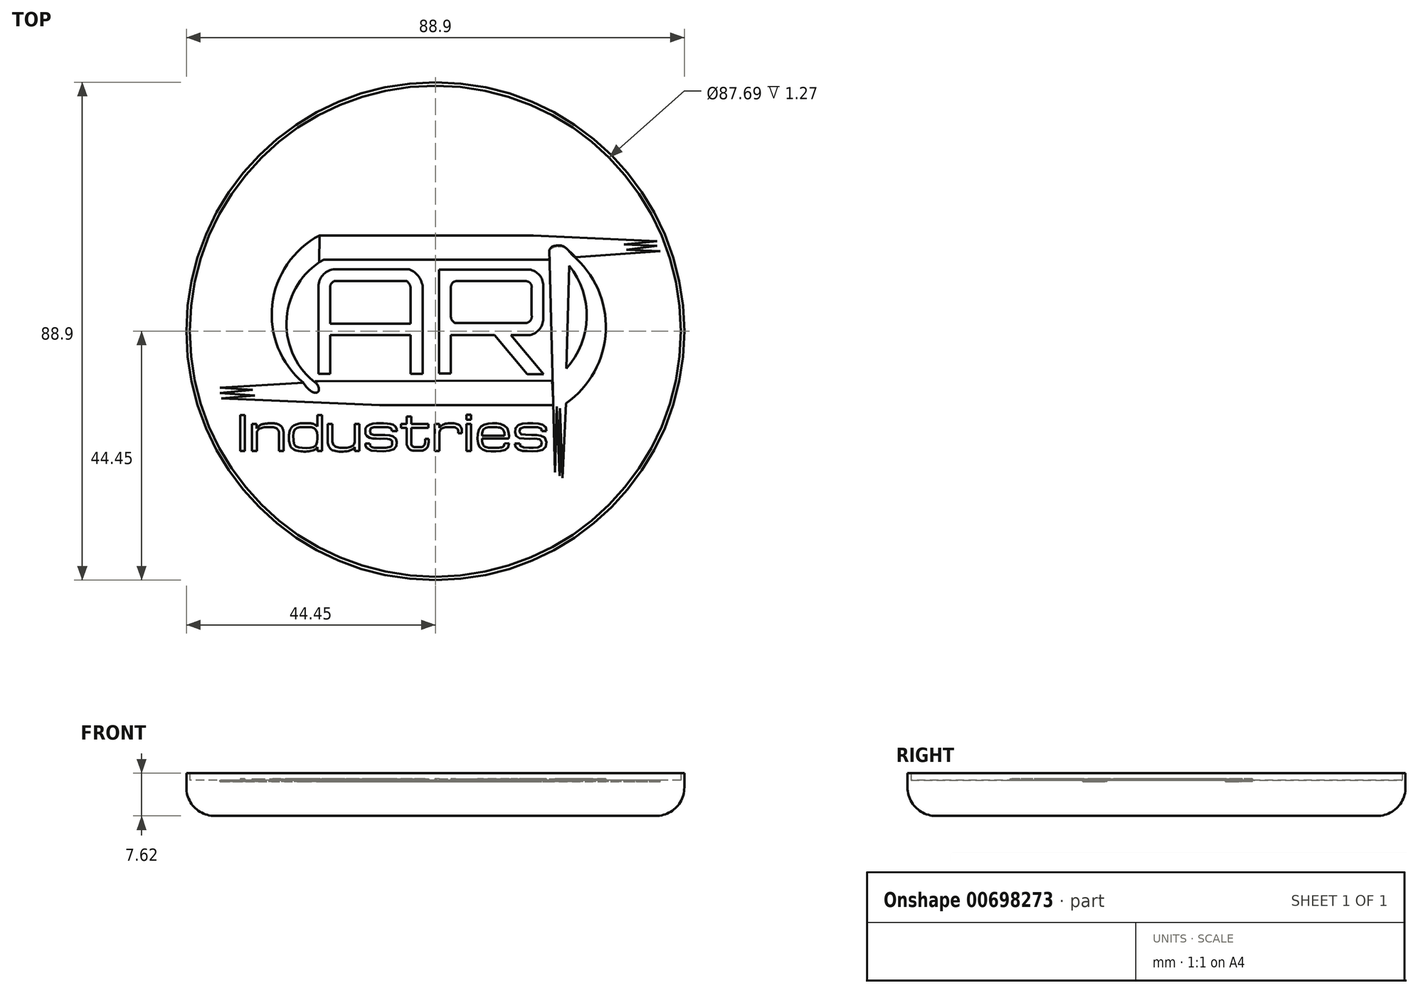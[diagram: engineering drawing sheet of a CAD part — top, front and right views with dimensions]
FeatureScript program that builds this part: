
annotation { "Feature Type Name" : "Feature", "Feature Type Description" : "" }
export const myFeature = defineFeature(function(context is Context, id is Id, definition is map)
    precondition{}
    {
        {
            var Q0;
            Q0=qCreatedBy(makeId("Top.planeOp"),FACE);
            var sketch = newSketch(context, id + "F0", { "sketchPlane" : qUnion([Q0])});
            skCircle(sketch, "E0", {"center": v(0, 0) * mm, "radius": 44.45 * mm});
            skSolve(sketch);
        }
        {
            var Q0;
            Q0=makeQuery(id+"F0.imprint","IMPRINT",FACE,{"disambiguationData":[TD([[makeQuery(id+"F0.imprint","IMPRINT",EDGE,{"derivedFrom":sQuery(id+"F0.wireOp",EDGE,"E0")}),1.0]])]});
            var Q1;
            Q1 = qSketchRegion(id + "FZvUu5gdxCIZSAn_1", true);
            extrude(context, id + "F1", {"entities" : qUnion([Q0, Q1]), "depth" : 6.35 * mm, "offsetDistance" : 25.4 * mm});
        }
        {
            var Q0;
            Q0=makeQuery(id+"F1.opExtrude","CAP_FACE",FACE,{"disambiguationData":[OSD([sQuery(id+"F0.wireOp",EDGE,"E0")])],"isStart":false});
            var sketch = newSketch(context, id + "F2", { "sketchPlane" : qUnion([Q0])});
            skLineSegment(sketch, "E1", {"start": v(-20.68, 17.1) * mm, "end": v(3.27, 17.1) * mm});
            skLineSegment(sketch, "E2", {"start": v(3.27, 17.1) * mm, "end": v(17.5, 17.1) * mm});
            skLineSegment(sketch, "E3", {"start": v(17.5, 17.1) * mm, "end": v(39.6, 16.1) * mm});
            skLineSegment(sketch, "E4", {"start": v(39.6, 16.1) * mm, "end": v(33.68, 15.49) * mm});
            skLineSegment(sketch, "E5", {"start": v(33.68, 15.49) * mm, "end": v(39.6, 15.22) * mm});
            skLineSegment(sketch, "E6", {"start": v(39.6, 15.22) * mm, "end": v(34.13, 14.55) * mm});
            skLineSegment(sketch, "E7", {"start": v(34.13, 14.55) * mm, "end": v(40.17, 14.28) * mm});
            skLineSegment(sketch, "E8", {"start": v(40.17, 14.28) * mm, "end": v(25.05, 13.22) * mm});
            skLineSegment(sketch, "E9", {"start": v(21.09, -13.18) * mm, "end": v(-9.93, -13.18) * mm});
            skLineSegment(sketch, "E10", {"start": v(-9.93, -13.18) * mm, "end": v(-38.2, -12.01) * mm});
            skLineSegment(sketch, "E11", {"start": v(-38.2, -12.01) * mm, "end": v(-32.22, -11.47) * mm});
            skLineSegment(sketch, "E12", {"start": v(-32.22, -11.47) * mm, "end": v(-38.47, -11.07) * mm});
            skLineSegment(sketch, "E13", {"start": v(-38.47, -11.07) * mm, "end": v(-32.61, -10.5) * mm});
            skLineSegment(sketch, "E14", {"start": v(-32.61, -10.5) * mm, "end": v(-38.47, -10.12) * mm});
            skLineSegment(sketch, "E15", {"start": v(-38.47, -10.12) * mm, "end": v(-23.55, -9.23) * mm});
            skLineSegment(sketch, "E16", {"start": v(-19.94, 12.8) * mm, "end": v(20.37, 12.8) * mm});
            skLineSegment(sketch, "E17", {"start": v(20.88, -8.84) * mm, "end": v(-20.9, -8.96) * mm});
            skLineSegment(sketch, "E18", {"start": v(-20.9, -8.96) * mm, "end": v(-21.48, -8.96) * mm});
            skFitSpline(sketch, "E19", {"points": [v(-23.55, -9.23) * mm, v(-23.04, -9.94) * mm, v(-22.45, -10.52) * mm, v(-21.73, -10.94) * mm, v(-21.12, -10.94) * mm, v(-20.8, -10.55) * mm, v(-20.83, -10.06) * mm, v(-21.15, -9.42) * mm, v(-21.48, -8.96) * mm], "startDerivative": vector(3.5, -5.09) * mm, "endDerivative": vector(-0.03, 4.48) * mm});
            skFitSpline(sketch, "E20", {"points": [v(-20.71, 12.3) * mm, v(-19.94, 12.8) * mm], "startDerivative": vector(0.78, 0.5) * mm, "endDerivative": vector(0.78, 0.5) * mm});
            skLineSegment(sketch, "E21", {"start": v(-20.68, 17.1) * mm, "end": v(-20.71, 12.3) * mm});
            skLineSegment(sketch, "E22", {"start": v(20.88, -8.84) * mm, "end": v(21.09, -13.18) * mm});
            skLineSegment(sketch, "E23", {"start": v(20.37, 12.8) * mm, "end": v(20.37, 14.57) * mm});
            skFitSpline(sketch, "E24", {"points": [v(25.05, 13.22) * mm, v(23.55, 14.57) * mm, v(22.5, 15.06) * mm, v(21.77, 15.06) * mm, v(21.45, 15.06) * mm, v(20.37, 14.57) * mm], "startDerivative": vector(-5.42, 5.3) * mm, "endDerivative": vector(-5.79, -3.03) * mm});
            skSolve(sketch);
        }
        {
            var Q0;
            Q0 = qSketchRegion(id + "F2", true);
            extrude(context, id + "F3", {"entities" : qUnion([Q0]), "operationType" : NewBodyOperationType.REMOVE, "oppositeDirection" : true, "depth" : 0.25 * mm, "offsetDistance" : 25.4 * mm});
        }
        {
            var Q0;
            Q0=makeQuery(id+"F1.opExtrude","CAP_FACE",FACE,{"disambiguationData":[OSD([sQuery(id+"F0.wireOp",EDGE,"E0")])],"isStart":false});
            var sketch = newSketch(context, id + "F4", { "sketchPlane" : qUnion([Q0])});
            skLineSegment(sketch, "E25", {"start": v(-18.77, 1.36) * mm, "end": v(-4.4, 1.36) * mm});
            skLineSegment(sketch, "E26", {"start": v(-4.4, 1.36) * mm, "end": v(-4.4, 7.49) * mm});
            skLineSegment(sketch, "E27", {"start": v(-18.77, 1.36) * mm, "end": v(-18.77, 7.88) * mm});
            skLineSegment(sketch, "E28", {"start": v(-18.77, -0.72) * mm, "end": v(-4.4, -0.72) * mm});
            skLineSegment(sketch, "E29", {"start": v(-4.4, -0.72) * mm, "end": v(-4.4, -7.63) * mm});
            skLineSegment(sketch, "E30", {"start": v(-18.77, -0.72) * mm, "end": v(-18.77, -7.63) * mm});
            skLineSegment(sketch, "E31", {"start": v(-18.77, -7.63) * mm, "end": v(-20.85, -7.63) * mm});
            skLineSegment(sketch, "E32", {"start": v(-20.85, -7.63) * mm, "end": v(-20.85, 7.97) * mm});
            skLineSegment(sketch, "E33", {"start": v(-4.4, -7.63) * mm, "end": v(-2.24, -7.63) * mm});
            skLineSegment(sketch, "E34", {"start": v(-2.24, -7.63) * mm, "end": v(-2.24, 7.54) * mm});
            skLineSegment(sketch, "E35", {"start": v(-18.02, 8.94) * mm, "end": v(-5.08, 8.94) * mm});
            skLineSegment(sketch, "E36", {"start": v(-4.67, 11.06) * mm, "end": v(-18.22, 11.06) * mm});
            skArc(sketch, "E37", {"start": v(-18.22, 11.06) * mm, "mid": v(-20.1, 10) * mm, "end": v(-20.85, 7.97) * mm});
            skArc(sketch, "E38", {"start": v(-2.24, 7.54) * mm, "mid": v(-2.9, 9.68) * mm, "end": v(-4.67, 11.06) * mm});
            skArc(sketch, "E39", {"start": v(-18.02, 8.94) * mm, "mid": v(-18.56, 8.53) * mm, "end": v(-18.77, 7.88) * mm});
            skArc(sketch, "E40", {"start": v(-4.4, 7.49) * mm, "mid": v(-4.57, 8.3) * mm, "end": v(-5.08, 8.94) * mm});
            skLineSegment(sketch, "E41", {"start": v(0.66, -7.53) * mm, "end": v(0.66, 11.02) * mm});
            skLineSegment(sketch, "E42", {"start": v(0.66, 11.02) * mm, "end": v(16.82, 11.02) * mm});
            skLineSegment(sketch, "E43", {"start": v(0.66, -7.53) * mm, "end": v(2.78, -7.53) * mm});
            skLineSegment(sketch, "E44", {"start": v(2.78, -7.53) * mm, "end": v(2.78, -0.67) * mm});
            skLineSegment(sketch, "E45", {"start": v(2.78, -0.67) * mm, "end": v(10.6, -0.67) * mm});
            skLineSegment(sketch, "E46", {"start": v(10.6, -0.67) * mm, "end": v(16.44, -7.68) * mm});
            skLineSegment(sketch, "E47", {"start": v(16.44, -7.68) * mm, "end": v(19.3, -7.68) * mm});
            skLineSegment(sketch, "E48", {"start": v(19.3, -7.68) * mm, "end": v(13.47, -0.67) * mm});
            skLineSegment(sketch, "E49", {"start": v(13.47, -0.67) * mm, "end": v(16.92, -0.67) * mm});
            skLineSegment(sketch, "E50", {"start": v(19.27, 8.12) * mm, "end": v(19.27, 2.23) * mm});
            skLineSegment(sketch, "E51", {"start": v(3.6, 1.45) * mm, "end": v(16.07, 1.45) * mm});
            skLineSegment(sketch, "E52", {"start": v(3.67, 8.94) * mm, "end": v(16.17, 8.94) * mm});
            skLineSegment(sketch, "E53", {"start": v(2.78, 7.88) * mm, "end": v(2.78, 2.61) * mm});
            skLineSegment(sketch, "E54", {"start": v(17.2, 7.68) * mm, "end": v(17.2, 2.85) * mm});
            skArc(sketch, "E55", {"start": v(3.67, 8.94) * mm, "mid": v(3.03, 8.57) * mm, "end": v(2.78, 7.88) * mm});
            skArc(sketch, "E56", {"start": v(2.78, 2.61) * mm, "mid": v(3, 1.9) * mm, "end": v(3.6, 1.45) * mm});
            skArc(sketch, "E57", {"start": v(16.07, 1.45) * mm, "mid": v(16.97, 1.88) * mm, "end": v(17.2, 2.85) * mm});
            skArc(sketch, "E58", {"start": v(17.2, 7.68) * mm, "mid": v(16.98, 8.55) * mm, "end": v(16.17, 8.94) * mm});
            skArc(sketch, "E59", {"start": v(16.92, -0.67) * mm, "mid": v(18.61, 0.36) * mm, "end": v(19.27, 2.23) * mm});
            skArc(sketch, "E60", {"start": v(19.27, 8.12) * mm, "mid": v(18.58, 10.02) * mm, "end": v(16.82, 11.02) * mm});
            skLineSegment(sketch, "E61", {"start": v(20.33, 14.53) * mm, "end": v(21.4, -25.19) * mm});
            skFitSpline(sketch, "E62", {"points": [v(20.33, 14.53) * mm, v(20.8, 15.06) * mm, v(21.4, 15.26) * mm, v(22.3, 15.32) * mm, v(23.05, 15.06) * mm, v(23.66, 14.53) * mm, v(24.46, 13.6) * mm], "startDerivative": vector(2.83, 4) * mm, "endDerivative": vector(4.08, -4.92) * mm});
            skArc(sketch, "E63", {"start": v(23.33, -12.88) * mm, "mid": v(30.43, 0.08) * mm, "end": v(24.46, 13.6) * mm});
            skLineSegment(sketch, "E64", {"start": v(23.33, -12.88) * mm, "end": v(22.72, -26.2) * mm});
            skLineSegment(sketch, "E65", {"start": v(22.72, -26.2) * mm, "end": v(22.27, -13.79) * mm});
            skLineSegment(sketch, "E66", {"start": v(22.16, -25.83) * mm, "end": v(22.27, -13.79) * mm});
            skLineSegment(sketch, "E67", {"start": v(22.16, -25.83) * mm, "end": v(21.71, -13.48) * mm});
            skLineSegment(sketch, "E68", {"start": v(21.71, -13.48) * mm, "end": v(21.4, -25.19) * mm});
            skArc(sketch, "E69", {"start": v(-20.71, 12.3) * mm, "mid": v(-26.58, 1.62) * mm, "end": v(-21.23, -9.33) * mm});
            skArc(sketch, "E70", {"start": v(-20.68, 17.1) * mm, "mid": v(-29.12, 4.7) * mm, "end": v(-23.55, -9.23) * mm});
            skLineSegment(sketch, "E71", {"start": v(23.88, 11.71) * mm, "end": v(23.42, -6.67) * mm});
            skArc(sketch, "E72", {"start": v(23.42, -6.67) * mm, "mid": v(27.02, 2.44) * mm, "end": v(23.88, 11.71) * mm});
            skFitSpline(sketch, "E73", {"points": [v(-23.55, -9.23) * mm, v(-23.5, -9.32) * mm, v(-23.36, -9.5) * mm, v(-23.2, -9.72) * mm, v(-22.93, -10.06) * mm, v(-22.67, -10.33) * mm, v(-22.48, -10.5) * mm, v(-22.2, -10.71) * mm, v(-22.09, -10.78) * mm, v(-21.93, -10.87) * mm, v(-21.68, -10.96) * mm, v(-21.44, -11) * mm, v(-21.24, -10.98) * mm], "startDerivative": vector(1, -1.41) * mm, "endDerivative": vector(4.4, 0.6) * mm});
            skFitSpline(sketch, "E74", {"points": [v(-21.24, -10.98) * mm, v(-21.2, -10.97) * mm, v(-21.14, -10.95) * mm, v(-21.08, -10.92) * mm, v(-21.03, -10.9) * mm, v(-21, -10.86) * mm, v(-20.94, -10.8) * mm, v(-20.9, -10.76) * mm, v(-20.88, -10.73) * mm, v(-20.86, -10.7) * mm, v(-20.84, -10.66) * mm, v(-20.82, -10.61) * mm, v(-20.8, -10.56) * mm, v(-20.79, -10.5) * mm, v(-20.78, -10.46) * mm, v(-20.78, -10.42) * mm, v(-20.78, -10.37) * mm, v(-20.78, -10.33) * mm], "startDerivative": vector(0.82, 0.2) * mm, "endDerivative": vector(-0.02, 0.76) * mm});
            skFitSpline(sketch, "E75", {"points": [v(-20.78, -10.33) * mm, v(-20.78, -10.28) * mm, v(-20.8, -10.23) * mm, v(-20.8, -10.2) * mm, v(-20.8, -10.15) * mm, v(-20.82, -10.12) * mm, v(-20.83, -10.07) * mm, v(-20.84, -10.02) * mm, v(-20.86, -9.98) * mm, v(-20.88, -9.91) * mm, v(-20.9, -9.86) * mm, v(-20.92, -9.81) * mm, v(-20.92, -9.8) * mm, v(-20.94, -9.77) * mm, v(-20.96, -9.73) * mm, v(-20.98, -9.67) * mm, v(-21.01, -9.62) * mm, v(-21.04, -9.56) * mm, v(-21.07, -9.53) * mm, v(-21.1, -9.48) * mm, v(-21.14, -9.43) * mm, v(-21.17, -9.4) * mm, v(-21.2, -9.36) * mm, v(-21.23, -9.33) * mm], "startDerivative": vector(-0.1, 0.98) * mm, "endDerivative": vector(-0.64, 0.65) * mm});
            skFitSpline(sketch, "E76", {"points": [v(-20.68, 17.1) * mm, v(-20.68, 16.62) * mm, v(-20.69, 16) * mm, v(-20.7, 15.36) * mm, v(-20.7, 14.4) * mm, v(-20.7, 12.75) * mm, v(-20.71, 12.48) * mm, v(-20.71, 12.3) * mm], "startDerivative": vector(-0.03, -3.67) * mm, "endDerivative": vector(-0.02, -2.42) * mm});
            skSolve(sketch);
        }
        {
            var Q0;
            Q0 = qSketchRegion(id + "F4", true);
            extrude(context, id + "F5", {"entities" : qUnion([Q0]), "operationType" : NewBodyOperationType.ADD, "depth" : 0.25 * mm, "offsetDistance" : 25.4 * mm});
        }
        {
            var Q0;
            Q0=makeQuery(id+"F1.opExtrude","CAP_FACE",FACE,{"disambiguationData":[OSD([sQuery(id+"F0.wireOp",EDGE,"E0")])],"isStart":false});
            var sketch = newSketch(context, id + "F6", { "sketchPlane" : qUnion([Q0])});
            skLineSegment(sketch, "E77", {"start": v(-34.85, -21.38) * mm, "end": v(-34.85, -14.96) * mm});
            skLineSegment(sketch, "E78", {"start": v(-34.85, -14.96) * mm, "end": v(-33.98, -14.96) * mm});
            skLineSegment(sketch, "E79", {"start": v(-33.98, -14.96) * mm, "end": v(-33.98, -21.38) * mm});
            skLineSegment(sketch, "E80", {"start": v(-33.98, -21.38) * mm, "end": v(-34.85, -21.38) * mm});
            skLineSegment(sketch, "E81", {"start": v(-32.7, -16.6) * mm, "end": v(-31.9, -16.6) * mm});
            skLineSegment(sketch, "E82", {"start": v(-31.9, -16.6) * mm, "end": v(-31.9, -17.36) * mm});
            skLineSegment(sketch, "E83", {"start": v(-32.7, -16.6) * mm, "end": v(-32.7, -21.38) * mm});
            skLineSegment(sketch, "E84", {"start": v(-32.7, -21.38) * mm, "end": v(-31.87, -21.38) * mm});
            skLineSegment(sketch, "E85", {"start": v(-31.87, -21.38) * mm, "end": v(-31.87, -18.15) * mm});
            skPoint(sketch, "E86.2.internal.snap0", {"position": v(-31.9, -16.98) * mm});
            skFitSpline(sketch, "E86", {"points": [v(-31.9, -17.36) * mm, v(-31.73, -17.14) * mm, v(-31.54, -16.98) * mm, v(-31.28, -16.77) * mm, v(-30.94, -16.63) * mm, v(-30.5, -16.54) * mm, v(-29.97, -16.47) * mm, v(-29.48, -16.45) * mm], "startDerivative": vector(1.34, 1.97) * mm, "endDerivative": vector(3.55, -0.7) * mm});
            skFitSpline(sketch, "E87", {"points": [v(-29.48, -16.45) * mm, v(-29.19, -16.45) * mm, v(-28.9, -16.45) * mm, v(-28.61, -16.48) * mm, v(-28.28, -16.55) * mm, v(-27.85, -16.73) * mm, v(-27.49, -17) * mm, v(-27.25, -17.4) * mm, v(-27.12, -17.9) * mm, v(-27.1, -18.05) * mm], "startDerivative": vector(2.88, -0.02) * mm, "endDerivative": vector(0.29, -1.67) * mm});
            skFitSpline(sketch, "E88", {"points": [v(-31.87, -18.15) * mm, v(-31.83, -17.95) * mm, v(-31.72, -17.74) * mm, v(-31.59, -17.57) * mm, v(-31.28, -17.35) * mm, v(-30.93, -17.23) * mm, v(-30.62, -17.16) * mm, v(-30.06, -17.14) * mm, v(-29.44, -17.14) * mm, v(-29.03, -17.15) * mm, v(-28.76, -17.19) * mm, v(-28.4, -17.33) * mm, v(-28.16, -17.52) * mm, v(-28.03, -17.7) * mm, v(-27.92, -18.04) * mm, v(-27.9, -18.15) * mm], "startDerivative": vector(0.57, 3.72) * mm, "endDerivative": vector(0.27, -2.24) * mm});
            skLineSegment(sketch, "E89", {"start": v(-27.9, -18.15) * mm, "end": v(-27.9, -21.38) * mm});
            skLineSegment(sketch, "E90", {"start": v(-27.9, -21.38) * mm, "end": v(-27.1, -21.38) * mm});
            skLineSegment(sketch, "E91", {"start": v(-27.1, -21.38) * mm, "end": v(-27.1, -18.05) * mm});
            skLineSegment(sketch, "E92", {"start": v(-21.05, -20.7) * mm, "end": v(-21.05, -21.38) * mm});
            skLineSegment(sketch, "E93", {"start": v(-21.05, -21.38) * mm, "end": v(-20.24, -21.38) * mm});
            skLineSegment(sketch, "E94", {"start": v(-20.24, -21.38) * mm, "end": v(-20.24, -14.99) * mm});
            skLineSegment(sketch, "E95", {"start": v(-20.24, -14.99) * mm, "end": v(-21.05, -14.99) * mm});
            skLineSegment(sketch, "E96", {"start": v(-21.05, -14.99) * mm, "end": v(-21.05, -17.01) * mm});
            skArc(sketch, "E97", {"start": v(-21.05, -17.01) * mm, "mid": v(-21.78, -16.57) * mm, "end": v(-22.62, -16.46) * mm});
            skLineSegment(sketch, "E98", {"start": v(-22.62, -16.46) * mm, "end": v(-23.76, -16.46) * mm});
            skFitSpline(sketch, "E99", {"points": [v(-23.76, -16.46) * mm, v(-24.06, -16.46) * mm, v(-24.51, -16.53) * mm, v(-24.87, -16.65) * mm, v(-25.16, -16.77) * mm, v(-25.47, -16.97) * mm, v(-25.7, -17.21) * mm, v(-25.84, -17.48) * mm, v(-25.97, -17.78) * mm, v(-26.08, -18.23) * mm, v(-26.12, -18.65) * mm, v(-26.12, -19.1) * mm, v(-26.11, -19.6) * mm], "startDerivative": vector(-3.77, 0.16) * mm, "endDerivative": vector(-0.26, -4.85) * mm});
            skFitSpline(sketch, "E100", {"points": [v(-26.11, -19.6) * mm, v(-26.05, -19.97) * mm, v(-25.93, -20.39) * mm, v(-25.66, -20.82) * mm, v(-25.17, -21.18) * mm, v(-24.56, -21.37) * mm, v(-23.77, -21.47) * mm, v(-23.19, -21.5) * mm, v(-22.56, -21.46) * mm, v(-22.02, -21.32) * mm, v(-21.5, -21.14) * mm, v(-21.19, -20.87) * mm, v(-21.05, -20.7) * mm], "startDerivative": vector(0.84, -5.24) * mm, "endDerivative": vector(2.18, 3.02) * mm});
            skFitSpline(sketch, "E101", {"points": [v(-24.16, -17.16) * mm, v(-23.2, -17.14) * mm, v(-22.46, -17.12) * mm, v(-22, -17.17) * mm, v(-21.62, -17.33) * mm, v(-21.36, -17.57) * mm, v(-21.19, -17.9) * mm, v(-21.1, -18.35) * mm, v(-21.05, -18.85) * mm, v(-21.05, -19.34) * mm, v(-21.14, -19.96) * mm, v(-21.39, -20.43) * mm, v(-21.75, -20.7) * mm, v(-22.38, -20.85) * mm, v(-23.12, -20.87) * mm, v(-24.08, -20.83) * mm, v(-24.5, -20.75) * mm, v(-25.01, -20.47) * mm, v(-25.27, -20.03) * mm, v(-25.34, -19.18) * mm, v(-25.34, -18.43) * mm, v(-25.27, -17.9) * mm, v(-25.01, -17.5) * mm, v(-24.64, -17.26) * mm, v(-24.16, -17.16) * mm]});
            skLineSegment(sketch, "E102", {"start": v(-12.5, -20.05) * mm, "end": v(-11.7, -20.05) * mm});
            skLineSegment(sketch, "E103", {"start": v(-7.71, -17.84) * mm, "end": v(-6.85, -17.84) * mm});
            skFitSpline(sketch, "E104", {"points": [v(-12.5, -20.05) * mm, v(-12.5, -20.22) * mm, v(-12.5, -20.41) * mm], "startDerivative": vector(0, -0.43) * mm, "endDerivative": vector(0, -0.53) * mm});
            skFitSpline(sketch, "E105", {"points": [v(-12.5, -20.41) * mm, v(-12.4, -20.6) * mm, v(-12.26, -20.84) * mm, v(-11.65, -21.23) * mm, v(-10.81, -21.4) * mm, v(-9.83, -21.44) * mm, v(-8.64, -21.4) * mm, v(-7.8, -21.26) * mm, v(-7.3, -21.02) * mm, v(-6.98, -20.61) * mm, v(-6.9, -20.04) * mm, v(-6.9, -19.72) * mm, v(-6.95, -19.39) * mm, v(-7.16, -19.05) * mm, v(-7.52, -18.78) * mm, v(-7.85, -18.65) * mm, v(-8.27, -18.58) * mm, v(-8.9, -18.56) * mm, v(-9.83, -18.54) * mm, v(-10.74, -18.52) * mm, v(-11.2, -18.48) * mm, v(-11.48, -18.4) * mm, v(-11.64, -18.23) * mm, v(-11.67, -17.94) * mm, v(-11.67, -17.65) * mm, v(-11.57, -17.42) * mm, v(-11.34, -17.26) * mm, v(-11.05, -17.17) * mm, v(-10.42, -17.14) * mm, v(-9.88, -17.13) * mm, v(-9.2, -17.14) * mm, v(-8.65, -17.15) * mm, v(-8.24, -17.2) * mm, v(-7.93, -17.31) * mm, v(-7.74, -17.54) * mm, v(-7.71, -17.84) * mm], "startDerivative": vector(5.04, -9.49) * mm, "endDerivative": vector(-0.58, -13.71) * mm});
            skFitSpline(sketch, "E106", {"points": [v(-6.85, -17.84) * mm, v(-6.85, -17.7) * mm, v(-6.9, -17.42) * mm, v(-7.03, -17.14) * mm, v(-7.33, -16.83) * mm, v(-7.6, -16.7) * mm, v(-8.08, -16.55) * mm, v(-8.51, -16.5) * mm, v(-8.96, -16.47) * mm, v(-9.72, -16.46) * mm, v(-10.27, -16.45) * mm, v(-10.7, -16.47) * mm, v(-11.32, -16.54) * mm, v(-11.77, -16.7) * mm, v(-12.1, -16.9) * mm, v(-12.36, -17.19) * mm, v(-12.5, -17.47) * mm, v(-12.5, -17.84) * mm, v(-12.5, -18.25) * mm, v(-12.42, -18.5) * mm, v(-12.2, -18.78) * mm, v(-11.81, -19.03) * mm, v(-11.27, -19.15) * mm, v(-10.79, -19.2) * mm, v(-10.16, -19.2) * mm, v(-9.5, -19.2) * mm, v(-8.83, -19.2) * mm, v(-8.45, -19.24) * mm, v(-8.25, -19.27) * mm, v(-7.93, -19.37) * mm, v(-7.79, -19.5) * mm], "startDerivative": vector(0.37, 6.56) * mm, "endDerivative": vector(3.58, -6.96) * mm});
            skFitSpline(sketch, "E107", {"points": [v(-7.79, -19.5) * mm, v(-7.74, -19.57) * mm, v(-7.7, -19.72) * mm, v(-7.7, -20) * mm, v(-7.7, -20.22) * mm, v(-7.79, -20.45) * mm, v(-7.97, -20.63) * mm, v(-8.39, -20.75) * mm, v(-8.96, -20.8) * mm, v(-9.6, -20.83) * mm, v(-10.24, -20.83) * mm, v(-10.7, -20.82) * mm, v(-11.16, -20.74) * mm, v(-11.44, -20.62) * mm, v(-11.62, -20.4) * mm, v(-11.66, -20.2) * mm, v(-11.7, -20.05) * mm], "startDerivative": vector(1.56, -1.96) * mm, "endDerivative": vector(-1.06, 3.3) * mm});
            skLineSegment(sketch, "E108", {"start": v(-4.27, -20.02) * mm, "end": v(-4.27, -17.25) * mm});
            skLineSegment(sketch, "E109", {"start": v(-4.27, -17.25) * mm, "end": v(-1.27, -17.25) * mm});
            skLineSegment(sketch, "E110", {"start": v(-1.27, -17.25) * mm, "end": v(-1.27, -16.57) * mm});
            skLineSegment(sketch, "E111", {"start": v(-1.27, -16.57) * mm, "end": v(-4.27, -16.57) * mm});
            skLineSegment(sketch, "E112", {"start": v(-4.27, -16.57) * mm, "end": v(-4.27, -15.23) * mm});
            skLineSegment(sketch, "E113", {"start": v(-4.27, -15.23) * mm, "end": v(-5.09, -15.23) * mm});
            skLineSegment(sketch, "E114", {"start": v(-5.09, -15.23) * mm, "end": v(-5.09, -16.55) * mm});
            skLineSegment(sketch, "E115", {"start": v(-5.09, -16.55) * mm, "end": v(-6.12, -16.55) * mm});
            skLineSegment(sketch, "E116", {"start": v(-6.12, -16.55) * mm, "end": v(-6.12, -17.26) * mm});
            skLineSegment(sketch, "E117", {"start": v(-6.12, -17.26) * mm, "end": v(-5.09, -17.26) * mm});
            skLineSegment(sketch, "E118", {"start": v(-5.09, -17.26) * mm, "end": v(-5.09, -20) * mm});
            skLineSegment(sketch, "E119", {"start": v(-1.83, -19.27) * mm, "end": v(-1.16, -19.27) * mm});
            skFitSpline(sketch, "E120", {"points": [v(-1.83, -19.27) * mm, v(-1.83, -19.65) * mm, v(-1.83, -19.98) * mm, v(-1.92, -20.27) * mm, v(-2.07, -20.5) * mm, v(-2.37, -20.67) * mm, v(-2.82, -20.7) * mm, v(-3.66, -20.69) * mm, v(-4, -20.6) * mm, v(-4.2, -20.4) * mm, v(-4.27, -20.02) * mm], "startDerivative": vector(-0.08, -4) * mm, "endDerivative": vector(-0.25, 4.1) * mm});
            skFitSpline(sketch, "E121", {"points": [v(-5.09, -20) * mm, v(-5.09, -20.22) * mm], "startDerivative": vector(0, -0.25) * mm, "endDerivative": vector(0, -0.25) * mm});
            skFitSpline(sketch, "E122", {"points": [v(-5.09, -20.22) * mm, v(-5.02, -20.45) * mm, v(-4.9, -20.73) * mm, v(-4.76, -20.95) * mm, v(-4.43, -21.2) * mm, v(-3.98, -21.32) * mm, v(-3.57, -21.35) * mm, v(-3.18, -21.36) * mm, v(-2.75, -21.36) * mm, v(-2.4, -21.33) * mm, v(-1.93, -21.2) * mm, v(-1.55, -20.9) * mm, v(-1.33, -20.56) * mm, v(-1.2, -19.99) * mm, v(-1.16, -19.58) * mm, v(-1.16, -19.41) * mm], "startDerivative": vector(1.06, -4.22) * mm, "endDerivative": vector(0.12, 3.47) * mm});
            skLineSegment(sketch, "E123", {"start": v(-1.16, -19.27) * mm, "end": v(-1.16, -19.41) * mm});
            skLineSegment(sketch, "E124", {"start": v(0.76, -17.25) * mm, "end": v(0.76, -16.57) * mm});
            skLineSegment(sketch, "E125", {"start": v(0.76, -16.57) * mm, "end": v(-0.1, -16.57) * mm});
            skLineSegment(sketch, "E126", {"start": v(-0.1, -16.57) * mm, "end": v(-0.1, -21.4) * mm});
            skLineSegment(sketch, "E127", {"start": v(-0.1, -21.4) * mm, "end": v(0.76, -21.4) * mm});
            skLineSegment(sketch, "E128", {"start": v(0.76, -21.4) * mm, "end": v(0.76, -18.2) * mm});
            skFitSpline(sketch, "E129", {"points": [v(0.76, -18.2) * mm, v(0.76, -17.96) * mm, v(0.86, -17.73) * mm, v(1.05, -17.47) * mm, v(1.42, -17.27) * mm, v(1.75, -17.17) * mm, v(2.21, -17.14) * mm, v(2.74, -17.14) * mm, v(3.2, -17.14) * mm, v(3.67, -17.24) * mm, v(3.99, -17.48) * mm, v(4.07, -17.78) * mm, v(4.08, -18.2) * mm], "startDerivative": vector(-0.38, 3.74) * mm, "endDerivative": vector(-0.01, -5) * mm});
            skLineSegment(sketch, "E130", {"start": v(4.08, -18.2) * mm, "end": v(4.74, -18.2) * mm});
            skFitSpline(sketch, "E131", {"points": [v(0.76, -17.25) * mm, v(0.89, -17.04) * mm, v(1.14, -16.81) * mm, v(1.42, -16.66) * mm, v(1.87, -16.52) * mm, v(2.28, -16.46) * mm, v(2.67, -16.45) * mm, v(3.18, -16.45) * mm, v(3.6, -16.49) * mm, v(4.04, -16.63) * mm, v(4.4, -16.86) * mm, v(4.6, -17.17) * mm, v(4.72, -17.53) * mm, v(4.74, -17.94) * mm, v(4.74, -18.2) * mm], "startDerivative": vector(1.89, 3.7) * mm, "endDerivative": vector(-0.02, -4.11) * mm});
            skLineSegment(sketch, "E132.bottom", {"start": v(5.54, -16.57) * mm, "end": v(6.36, -16.57) * mm});
            skLineSegment(sketch, "E132.top", {"start": v(5.54, -21.4) * mm, "end": v(6.36, -21.4) * mm});
            skLineSegment(sketch, "E132.left", {"start": v(5.54, -16.57) * mm, "end": v(5.54, -21.4) * mm});
            skLineSegment(sketch, "E132.right", {"start": v(6.36, -16.57) * mm, "end": v(6.36, -21.4) * mm});
            skLineSegment(sketch, "E133.bottom", {"start": v(5.53, -14.94) * mm, "end": v(6.36, -14.94) * mm});
            skLineSegment(sketch, "E133.top", {"start": v(5.53, -15.8) * mm, "end": v(6.36, -15.8) * mm});
            skLineSegment(sketch, "E133.left", {"start": v(5.53, -14.94) * mm, "end": v(5.53, -15.8) * mm});
            skLineSegment(sketch, "E133.right", {"start": v(6.36, -14.94) * mm, "end": v(6.36, -15.8) * mm});
            skLineSegment(sketch, "E134", {"start": v(8.37, -18.64) * mm, "end": v(12.33, -18.64) * mm});
            skFitSpline(sketch, "E135", {"points": [v(8.37, -18.64) * mm, v(8.37, -18.47) * mm, v(8.37, -18.19) * mm, v(8.42, -17.93) * mm, v(8.56, -17.58) * mm, v(8.77, -17.4) * mm, v(9.1, -17.23) * mm, v(9.4, -17.17) * mm, v(9.83, -17.14) * mm, v(10.32, -17.13) * mm, v(10.78, -17.13) * mm, v(11.2, -17.17) * mm, v(11.65, -17.26) * mm, v(11.96, -17.48) * mm, v(12.21, -17.76) * mm, v(12.33, -18.09) * mm, v(12.34, -18.36) * mm, v(12.33, -18.64) * mm], "startDerivative": vector(0.04, 3.85) * mm, "endDerivative": vector(-0.36, -5.32) * mm});
            skLineSegment(sketch, "E136", {"start": v(13.13, -19.2) * mm, "end": v(8.37, -19.2) * mm});
            skFitSpline(sketch, "E137", {"points": [v(13.13, -19.2) * mm, v(13.18, -18.97) * mm, v(13.13, -18.41) * mm, v(13.06, -17.9) * mm, v(12.91, -17.48) * mm, v(12.64, -17.11) * mm, v(12.13, -16.74) * mm, v(11.52, -16.52) * mm, v(10.97, -16.46) * mm, v(10.38, -16.44) * mm, v(9.81, -16.46) * mm, v(9.09, -16.56) * mm, v(8.55, -16.75) * mm, v(8.18, -17) * mm, v(7.89, -17.38) * mm, v(7.65, -18) * mm, v(7.56, -18.82) * mm, v(7.57, -19.64) * mm, v(7.71, -20.3) * mm, v(7.98, -20.78) * mm, v(8.42, -21.15) * mm, v(8.9, -21.34) * mm, v(9.7, -21.45) * mm, v(10.45, -21.49) * mm, v(11.3, -21.47) * mm, v(12.08, -21.35) * mm, v(12.73, -21.1) * mm, v(13.05, -20.63) * mm, v(13.19, -20.02) * mm], "startDerivative": vector(2.84, 8.99) * mm, "endDerivative": vector(2.89, 16.46) * mm});
            skFitSpline(sketch, "E138", {"points": [v(8.37, -19.2) * mm, v(8.37, -19.38) * mm, v(8.37, -19.74) * mm, v(8.51, -20.23) * mm, v(8.77, -20.57) * mm, v(9.2, -20.76) * mm, v(9.88, -20.82) * mm, v(10.9, -20.83) * mm, v(11.7, -20.78) * mm, v(12.2, -20.57) * mm, v(12.35, -20.04) * mm], "startDerivative": vector(0.06, -2.87) * mm, "endDerivative": vector(0.73, 6) * mm});
            skLineSegment(sketch, "E139", {"start": v(12.35, -20.04) * mm, "end": v(13.19, -20.02) * mm});
            skLineSegment(sketch, "E140", {"start": v(14.2, -20.05) * mm, "end": v(15.07, -20.05) * mm});
            skLineSegment(sketch, "E141", {"start": v(19.03, -17.84) * mm, "end": v(19.86, -17.84) * mm});
            skFitSpline(sketch, "E142", {"points": [v(14.2, -20.05) * mm, v(14.2, -20.31) * mm, v(14.33, -20.7) * mm, v(14.71, -21.07) * mm, v(15.36, -21.34) * mm, v(15.95, -21.4) * mm, v(16.74, -21.44) * mm, v(17.39, -21.44) * mm, v(18.32, -21.37) * mm, v(19.13, -21.2) * mm, v(19.65, -20.8) * mm, v(19.86, -20.2) * mm, v(19.75, -19.29) * mm, v(19.35, -18.85) * mm, v(18.75, -18.62) * mm, v(18.19, -18.54) * mm, v(17.47, -18.52) * mm, v(16.47, -18.5) * mm, v(15.54, -18.47) * mm, v(15.25, -18.38) * mm, v(15.09, -18.21) * mm, v(15.03, -17.78) * mm, v(15.13, -17.42) * mm, v(15.48, -17.22) * mm, v(16.03, -17.16) * mm, v(16.72, -17.15) * mm, v(17.44, -17.15) * mm, v(18.1, -17.16) * mm, v(18.53, -17.21) * mm, v(18.92, -17.4) * mm, v(19.03, -17.65) * mm, v(19.03, -17.84) * mm], "startDerivative": vector(-0.94, -12.62) * mm, "endDerivative": vector(-0.96, -9.5) * mm});
            skFitSpline(sketch, "E143", {"points": [v(15.07, -20.05) * mm, v(15.07, -20.26) * mm, v(15.15, -20.48) * mm, v(15.42, -20.7) * mm, v(15.89, -20.79) * mm, v(16.74, -20.83) * mm, v(17.3, -20.83) * mm, v(17.9, -20.8) * mm, v(18.4, -20.75) * mm, v(18.8, -20.57) * mm, v(19.03, -20.2) * mm, v(19, -19.8) * mm, v(18.9, -19.48) * mm, v(18.54, -19.28) * mm, v(17.7, -19.2) * mm, v(16.97, -19.22) * mm, v(16.1, -19.2) * mm, v(15.36, -19.15) * mm, v(14.79, -19) * mm, v(14.45, -18.74) * mm, v(14.3, -18.4) * mm, v(14.24, -17.97) * mm, v(14.25, -17.48) * mm, v(14.52, -16.96) * mm, v(14.95, -16.73) * mm, v(15.53, -16.54) * mm, v(16.23, -16.48) * mm, v(17.07, -16.45) * mm, v(17.88, -16.47) * mm, v(18.6, -16.51) * mm, v(19.18, -16.7) * mm, v(19.65, -17.01) * mm, v(19.8, -17.35) * mm, v(19.86, -17.84) * mm], "startDerivative": vector(-0.7, -10.9) * mm, "endDerivative": vector(0.97, -20.39) * mm});
            skLineSegment(sketch, "E144", {"start": v(-13.58, -21.38) * mm, "end": v(-13.58, -16.58) * mm});
            skLineSegment(sketch, "E145", {"start": v(-13.58, -16.58) * mm, "end": v(-14.39, -16.58) * mm});
            skLineSegment(sketch, "E146", {"start": v(-14.39, -16.58) * mm, "end": v(-14.39, -19.64) * mm});
            skLineSegment(sketch, "E147", {"start": v(-13.58, -21.38) * mm, "end": v(-14.39, -21.38) * mm});
            skLineSegment(sketch, "E148", {"start": v(-14.39, -21.38) * mm, "end": v(-14.39, -20.68) * mm});
            skLineSegment(sketch, "E149", {"start": v(-19.21, -16.58) * mm, "end": v(-18.37, -16.58) * mm});
            skLineSegment(sketch, "E150", {"start": v(-18.37, -16.58) * mm, "end": v(-18.37, -19.56) * mm});
            skLineSegment(sketch, "E151", {"start": v(-19.21, -16.58) * mm, "end": v(-19.21, -19.75) * mm});
            skFitSpline(sketch, "E152", {"points": [v(-18.37, -19.56) * mm, v(-18.37, -19.83) * mm, v(-18.23, -20.19) * mm, v(-18.1, -20.41) * mm, v(-17.7, -20.67) * mm, v(-17.2, -20.8) * mm, v(-16.64, -20.82) * mm, v(-16.02, -20.82) * mm, v(-15.64, -20.78) * mm, v(-15.21, -20.68) * mm, v(-14.79, -20.46) * mm, v(-14.53, -20.2) * mm, v(-14.41, -19.9) * mm, v(-14.39, -19.64) * mm], "startDerivative": vector(-0.44, -4.17) * mm, "endDerivative": vector(0.13, 4.2) * mm});
            skFitSpline(sketch, "E153", {"points": [v(-14.39, -20.68) * mm, v(-14.46, -20.79) * mm, v(-14.69, -21.03) * mm, v(-15.11, -21.24) * mm, v(-15.7, -21.42) * mm, v(-16.6, -21.51) * mm, v(-17.45, -21.48) * mm, v(-18.14, -21.33) * mm, v(-18.67, -21.09) * mm, v(-18.95, -20.68) * mm, v(-19.07, -20.42) * mm, v(-19.18, -20.1) * mm, v(-19.21, -19.75) * mm], "startDerivative": vector(-1.52, -2.23) * mm, "endDerivative": vector(-0.21, 5) * mm});
            skSolve(sketch);
        }
        {
            var Q0;
            Q0 = qSketchRegion(id + "F6", true);
            extrude(context, id + "F7", {"entities" : qUnion([Q0]), "operationType" : NewBodyOperationType.ADD, "depth" : 0.25 * mm, "offsetDistance" : 25.4 * mm});
        }
        {
            var Q0;
            Q0=makeQuery(id+"F1.opExtrude","CAP_FACE",FACE,{"disambiguationData":[OSD([sQuery(id+"F0.wireOp",EDGE,"E0")])],"isStart":false});
            var sketch = newSketch(context, id + "F8", { "sketchPlane" : qUnion([Q0])});
            skCircle(sketch, "E154", {"center": v(0, 0) * mm, "radius": 43.84 * mm});
            skCircle(sketch, "E155", {"center": v(0, 0) * mm, "radius": 44.45 * mm});
            skSolve(sketch);
        }
        {
            var Q0;
            Q0 = qSketchRegion(id + "F8", true);
            extrude(context, id + "F9", {"entities" : qUnion([Q0]), "operationType" : NewBodyOperationType.ADD, "depth" : 1.27 * mm, "offsetDistance" : 25.4 * mm});
        }
        {
            var Q0;
            Q0=makeQuery(id+"F1.opExtrude","CAP_EDGE",EDGE,{"disambiguationData":[OSD([sQuery(id+"F0.wireOp",EDGE,"E0")])],"isStart":true});
            fillet(context, id + "F10", {"entities" : qUnion([Q0]), "radius" : 5.08 * mm, "tangentPropagation" : true, "allowEdgeOverflow" : false});
        }
    });
